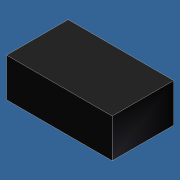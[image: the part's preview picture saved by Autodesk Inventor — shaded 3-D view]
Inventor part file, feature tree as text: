
AUTODESK INVENTOR PART (.ipt)
format: ipt  version: unknown  size: 166,400 bytes
history: native  units: mm
features: extrude x1, sketch x1
ambient origin geometry x8: Origin, YZ Plane, XZ Plane, XY Plane, X Axis, Y Axis, Z Axis, Center Point
feature tree (2):
  extrude  "Выдавливание2"  Depth=6.0mm
  sketch  "Эскиз2"
